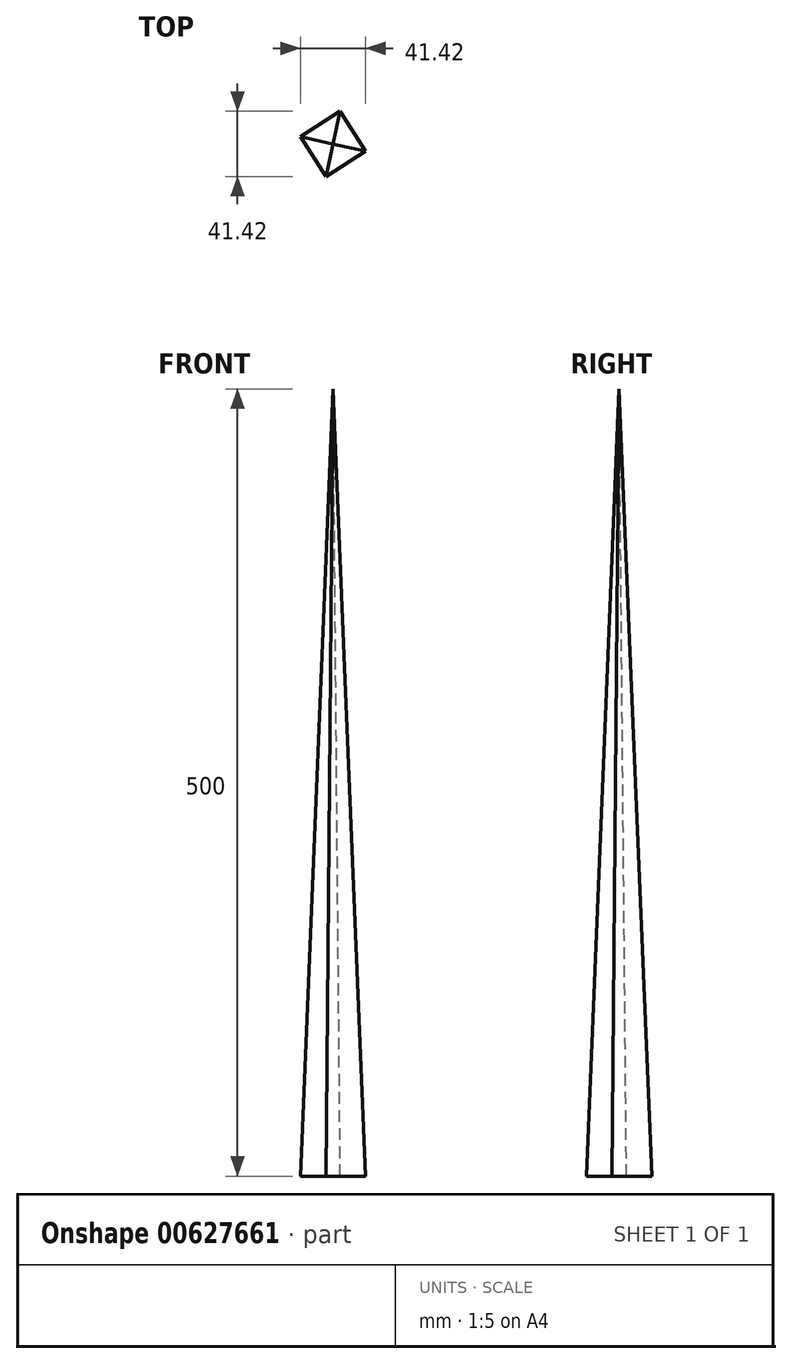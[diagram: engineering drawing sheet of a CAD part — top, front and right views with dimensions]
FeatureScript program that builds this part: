
annotation { "Feature Type Name" : "Feature", "Feature Type Description" : "" }
export const myFeature = defineFeature(function(context is Context, id is Id, definition is map)
    precondition{}
    {
        {
            var Q0;
            Q0=qCreatedBy(makeId("Top.planeOp"),FACE);
            var sketch = newSketch(context, id + "F0", { "sketchPlane" : qUnion([Q0])});
            skCircle(sketch, "E0.cCircle", {"center": v(0, 0) * mm, "radius": 15 * mm, "construction": true});
            skLineSegment(sketch, "E0.0", {"start": v(-4.58, -20.71) * mm, "end": v(-20.71, 4.58) * mm});
            skLineSegment(sketch, "E0.1", {"start": v(-20.71, 4.58) * mm, "end": v(4.58, 20.71) * mm});
            skLineSegment(sketch, "E0.2", {"start": v(4.58, 20.71) * mm, "end": v(20.71, -4.58) * mm});
            skLineSegment(sketch, "E0.3", {"start": v(20.71, -4.58) * mm, "end": v(-4.58, -20.71) * mm});
            skPoint(sketch, "E0.0.midPoint", {"position": v(-12.64, -8.07) * mm});
            skSolve(sketch);
        }
        {
            var Q0;
            Q0=qCreatedBy(makeId("Top.planeOp"),FACE);
            cPlane(context, id + "F1", {"entities" : qUnion([Q0]), "cplaneType" : CPlaneType.OFFSET, "offset" : 500 * mm, "width" : 150 * mm, "height" : 150 * mm});
        }
        {
            var Q0;
            Q0=qCreatedBy(id+"F1.planeOp",FACE);
            var sketch = newSketch(context, id + "F2", { "sketchPlane" : qUnion([Q0])});
            skPoint(sketch, "E1", {"position": v(0, 0) * mm});
            skSolve(sketch);
        }
        {
            var Q0;
            Q0=makeQuery(id+"F0.imprint","IMPRINT",FACE,{"disambiguationData":[TD([[makeQuery(id+"F0.imprint","IMPRINT",EDGE,{"derivedFrom":sQuery(id+"F0.wireOp",EDGE,"E0.0")}),-1.0]])]});
            var Q1;
            Q1=sQuery(id+"F2.wireOp",VERTEX,"E1");
            loft(context, id + "F3", {"sheetProfilesArray" : [{ "sheetProfileEntities" : qUnion([Q0]) }, { "sheetProfileEntities" : qUnion([Q1]) }]});
        }
    });
